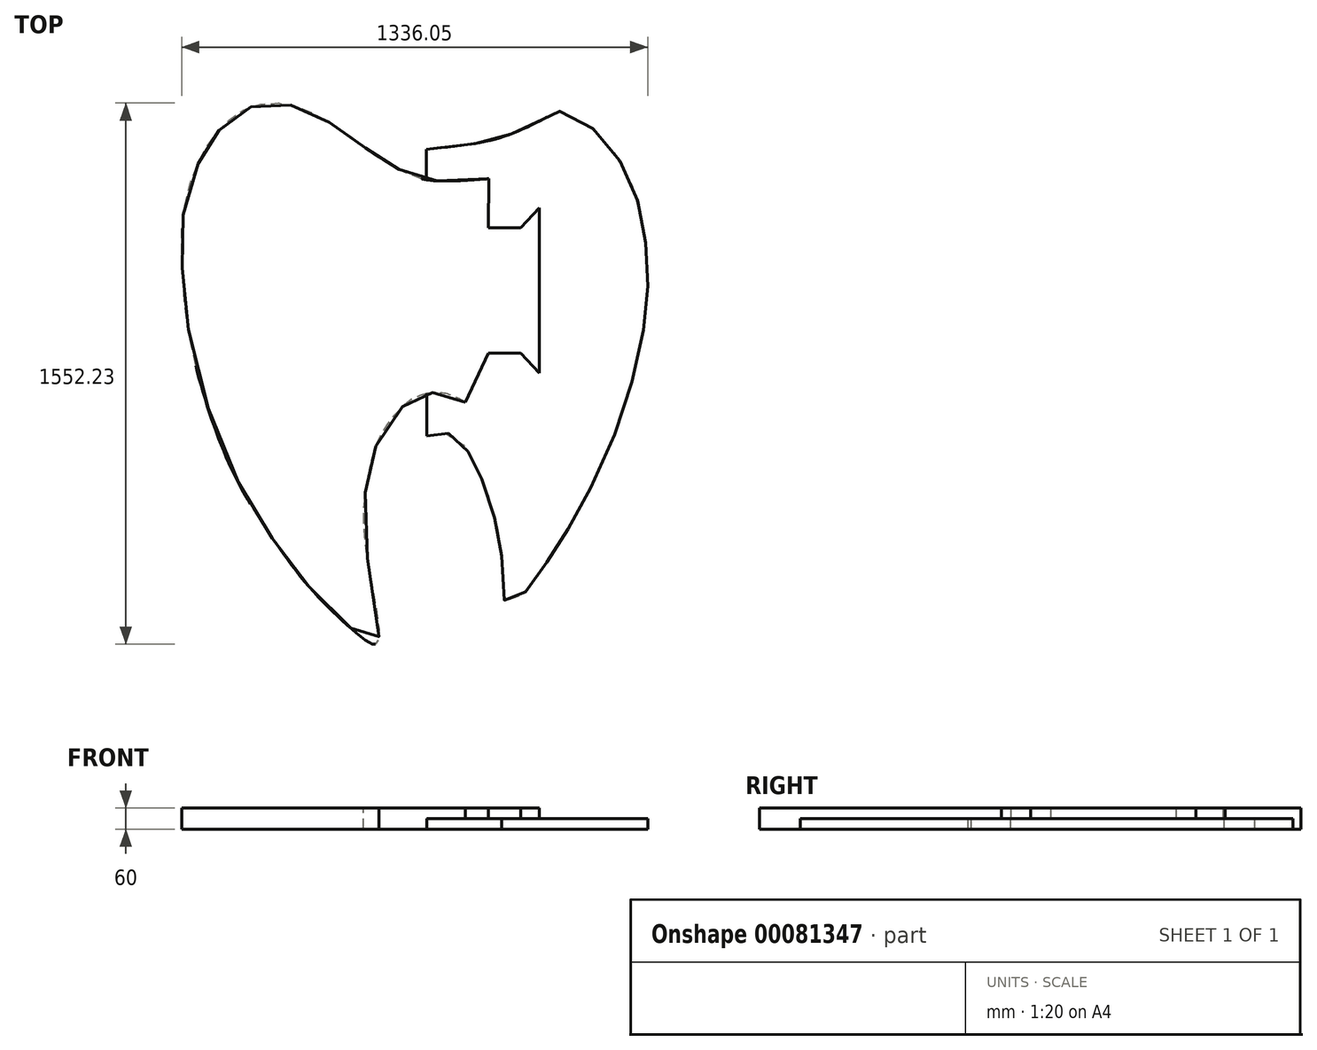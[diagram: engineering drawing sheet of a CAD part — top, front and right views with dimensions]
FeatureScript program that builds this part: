
annotation { "Feature Type Name" : "Feature", "Feature Type Description" : "" }
export const myFeature = defineFeature(function(context is Context, id is Id, definition is map)
    precondition{}
    {
        {
            var Q0;
            Q0=qCreatedBy(makeId("Top.planeOp"),FACE);
            var sketch = newSketch(context, id + "F0", { "sketchPlane" : qUnion([Q0])});
            skFitSpline(sketch, "E0", {"points": [v(131.96, -83.23) * mm, v(71.7, -58) * mm, v(9.47, -61.65) * mm, v(-42.11, -91.08) * mm, v(-114.72, -186.11) * mm, v(-148.68, -304.12) * mm, v(-156, -483.6) * mm, v(-121, -773.99) * mm, v(-175.45, -749.35) * mm, v(-306.38, -623.6) * mm, v(-428.24, -462.85) * mm, v(-551.4, -245.06) * mm, v(-659, 106.26) * mm, v(-679.74, 314.98) * mm, v(-674.56, 467.95) * mm, v(-629.18, 611.85) * mm, v(-586.4, 680.55) * mm, v(-526.77, 740.19) * mm, v(-445.1, 772.6) * mm, v(-358.24, 766.12) * mm, v(-270.09, 725.93) * mm, v(-172.86, 661.1) * mm, v(-115.82, 617.03) * mm, v(-31.55, 571.66) * mm, v(55.3, 550.92) * mm, v(199.2, 557.4) * mm, v(197.9, 557.4) * mm], "startDerivative": vector(-2057.54, 1113.53) * mm, "endDerivative": vector(-522.46, -16.62) * mm});
            skLineSegment(sketch, "E1", {"start": v(-24.8, 1210.26) * mm, "end": v(-24.8, -999.05) * mm, "construction": true});
            skPoint(sketch, "E2.endSnap0", {"position": v(198.6, 237.1) * mm});
            skLineSegment(sketch, "E3", {"start": v(198.6, 416.8) * mm, "end": v(290.9, 416.8) * mm, "construction": true});
            skLineSegment(sketch, "E4", {"start": v(198.6, 57.38) * mm, "end": v(290.9, 57.38) * mm, "construction": true});
            skLineSegment(sketch, "E5", {"start": v(290.9, 57.38) * mm, "end": v(343.53, 0) * mm});
            skLineSegment(sketch, "E6.MirrorCS", {"start": v(290.9, 416.8) * mm, "end": v(343.53, 474.19) * mm});
            skLineSegment(sketch, "E7", {"start": v(343.53, 474.19) * mm, "end": v(343.53, 0) * mm});
            skLineSegment(sketch, "E8", {"start": v(199.2, 557.4) * mm, "end": v(198.6, 416.8) * mm});
            skLineSegment(sketch, "E9", {"start": v(198.6, 416.8) * mm, "end": v(290.9, 416.8) * mm});
            skLineSegment(sketch, "E10", {"start": v(198.6, 57.38) * mm, "end": v(290.9, 57.38) * mm});
            skLineSegment(sketch, "E11", {"start": v(198.6, 57.38) * mm, "end": v(131.96, -83.23) * mm});
            skSolve(sketch);
        }
        {
            var Q0;
            Q0=qCreatedBy(makeId("Top.planeOp"),FACE);
            var sketch = newSketch(context, id + "F1", { "sketchPlane" : qUnion([Q0])});
            skFitSpline(sketch, "E12", {"points": [v(21.78, -180.5) * mm, v(51.11, -172.25) * mm, v(86.86, -174.08) * mm, v(124.45, -203.42) * mm, v(155.61, -256.58) * mm, v(185.86, -320.75) * mm, v(222.53, -439) * mm, v(236.28, -543.5) * mm, v(249.12, -658.09) * mm, v(287.62, -644.34) * mm, v(329.78, -593.92) * mm, v(395.78, -496.75) * mm, v(449.87, -406.92) * mm, v(543.37, -218.08) * mm, v(613.04, -13.66) * mm, v(648.79, 165.09) * mm, v(654.29, 289.76) * mm, v(641.45, 425.43) * mm, v(609.37, 540.93) * mm, v(538.79, 659.18) * mm, v(455.37, 728.85) * mm, v(390.28, 751.76) * mm, v(382.03, 745.35) * mm, v(344.45, 722.43) * mm, v(268.37, 687.6) * mm, v(180.36, 661.93) * mm, v(19.95, 641.76) * mm], "startDerivative": vector(1286.51, 437.48) * mm, "endDerivative": vector(-3413.02, -338.45) * mm});
            skLineSegment(sketch, "E13", {"start": v(19.95, 641.76) * mm, "end": v(21.78, -180.5) * mm});
            skSolve(sketch);
        }
        {
            var Q0;
            Q0=makeQuery(id+"F0.imprint","IMPRINT",FACE,{"disambiguationData":[TD([[makeQuery(id+"F0.imprint","IMPRINT",EDGE,{"derivedFrom":sQuery(id+"F0.wireOp",EDGE,"E5")}),1.0]])]});
            extrude(context, id + "F2", {"entities" : qUnion([Q0]), "depth" : 60 * mm, "offsetDistance" : 25 * mm});
        }
        {
            var Q0;
            Q0=makeQuery(id+"F1.imprint","IMPRINT",FACE,{"disambiguationData":[TD([[makeQuery(id+"F1.imprint","IMPRINT",EDGE,{"derivedFrom":sQuery(id+"F1.wireOp",EDGE,"E12")}),1.0]])]});
            extrude(context, id + "F3", {"entities" : qUnion([Q0]), "operationType" : NewBodyOperationType.ADD, "depth" : 30 * mm, "offsetDistance" : 25 * mm});
        }
    });
